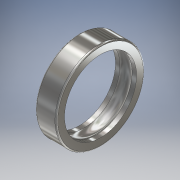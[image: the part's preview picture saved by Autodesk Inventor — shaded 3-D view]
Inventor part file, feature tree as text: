
AUTODESK INVENTOR PART (.ipt)
format: ipt  version: 2018 (Build 220112000, 112)  size: 160,256 bytes
history: native  units: mm
features: revolve x1, fillet x1, sketch x1
ambient origin geometry x8: Origin, YZ Plane, XZ Plane, XY Plane, X Axis, Y Axis, Z Axis, Center Point
bodies: Solid1 (feature_tree)
feature tree (3):
  revolve  "Revolution1"  [1 undecoded]
  fillet  "Fillet1"  Radius=12.0mm
  sketch  "Sketch1"  dims[d0=31.0mm d1=15.5mm d2=12.0mm d3=53.0mm d4=8.0mm d5=12.0mm d6=90.0deg d7=2.1mm]
note: 1 required parameter value undecoded (feature->parameter linkage not recoverable at this tier; creation-order binding heuristic only, values carry confidence <= 0.55)
